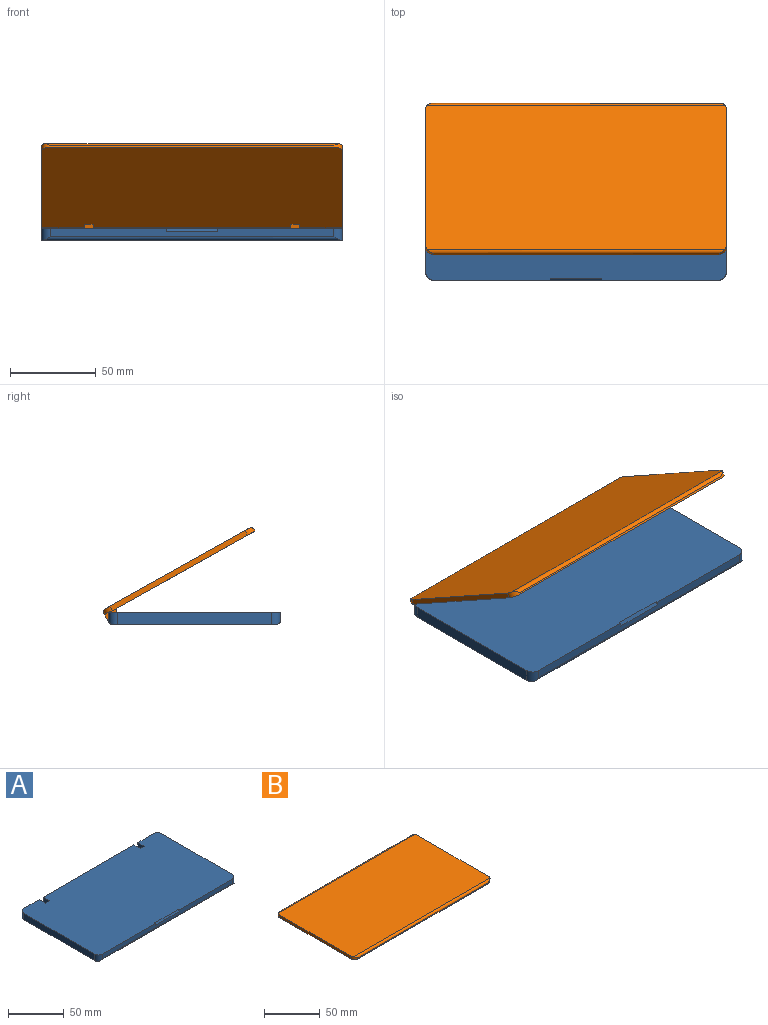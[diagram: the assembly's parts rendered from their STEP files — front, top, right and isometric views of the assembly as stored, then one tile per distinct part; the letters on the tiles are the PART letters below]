
ASSEMBLY  parts=2 mates=1
PART A: 52 faces, bbox 175x100x7 mm
  f0: plane 175x100mm, normal (0,0,1), area 17368.5mm2, adj f1,f2,f6,f7,f9,f11,f12,f13
  f1: plane 20x5mm, normal (0,1,0), area 100mm2, adj f0,f4,f12,f22
  f2: plane 115x5mm, normal (0,1,0), area 575mm2, adj f0,f3,f18,f23
  f3: cylinder r=2mm len=115mm, axis (-1,0,0), area 361.3mm2, adj f2,f10,f18,f23
  f4: cylinder r=2mm len=24mm, axis (-1,0,0), area 69.8mm2, adj f1,f10,f12,f22
  f5: cylinder r=2mm len=24mm, axis (-1,0,0), area 69.8mm2, adj f9,f10,f13,f19
  f6: plane 90x7mm, normal (1,0,0), area 630mm2, adj f0,f10,f13,f15
  f7: plane 165x5mm, normal (0,-1,0), area 765mm2, adj f0,f8,f14,f15,f24,f25,f26
  f8: cylinder r=2mm len=173mm, axis (-1,0,0), area 532.4mm2, adj f7,f10,f14,f15
  f9: plane 20x5mm, normal (0,1,0), area 100mm2, adj f0,f5,f13,f19
  f10: plane 175x96mm, normal (0,0,-1), area 16796.2mm2, adj f3,f4,f5,f6,f8,f11,f12,f13
  f11: plane 90x7mm, normal (-1,0,0), area 630mm2, adj f0,f10,f12,f14
  f12: cylinder r=5mm len=7mm, axis (0,0,1), area 51.4mm2, adj f0,f1,f4,f10,f11
  f13: cylinder r=5mm len=7mm, axis (0,0,1), area 51.4mm2, adj f0,f5,f6,f9,f10
  f14: cylinder r=5mm len=7mm, axis (0,0,1), area 51.4mm2, adj f0,f7,f8,f10,f11
  f15: cylinder r=5mm len=7mm, axis (0,0,1), area 51.4mm2, adj f0,f6,f7,f8,f10
  f16: cylinder r=2mm len=5mm, axis (-1,0,0), area 9.5mm2, adj f10,f17,f18,f19
  f17: plane 6.16x5mm, normal (0,0.82,0.58), area 37.7mm2, adj f0,f16,f18,f19
  f18: plane 8x7mm, normal (1,0,0), area 37.6mm2, adj f0,f2,f3,f16,f17
  f19: plane 8x7mm, normal (-1,0,0), area 37.6mm2, adj f0,f5,f9,f16,f17
  f20: cylinder r=2mm len=5mm, axis (-1,0,0), area 9.5mm2, adj f10,f21,f22,f23
  f21: plane 6.16x5mm, normal (0,0.82,0.58), area 37.7mm2, adj f0,f20,f22,f23
  f22: plane 8x7mm, normal (1,0,0), area 37.6mm2, adj f0,f1,f4,f20,f21
  f23: plane 8x7mm, normal (-1,0,0), area 37.6mm2, adj f0,f2,f3,f20,f21
  f24: plane 2x1mm, normal (-1,0,0), area 1mm2, adj f0,f7,f25
  f25: plane 30x2mm, normal (0,-0.89,0.45), area 67.1mm2, adj f0,f7,f24,f26
  f26: plane 2x1mm, normal (1,0,0), area 1mm2, adj f0,f7,f25
  f27: plane 173x96mm, normal (0,0,1), area 16561.4mm2, adj f31,f32,f33,f34,f36,f38,f39,f40
  f28: plane 173x98mm, normal (0,0,-1), area 16815.3mm2, adj f29,f30,f34,f35,f37,f38,f39,f40
  f29: plane 19x4mm, normal (0,-1,0), area 76mm2, adj f28,f32,f39,f47
  f30: plane 113x4mm, normal (0,-1,0), area 452mm2, adj f28,f31,f44,f48
  f31: cylinder r=1mm len=113mm, axis (-1,0,0), area 177.5mm2, adj f27,f30,f44,f48
  f32: cylinder r=1mm len=21.65mm, axis (-1,0,0), area 32.1mm2, adj f27,f29,f39,f47
  f33: cylinder r=1mm len=21.65mm, axis (-1,0,0), area 32.1mm2, adj f27,f37,f40,f45
  f34: plane 90x5mm, normal (-1,0,0), area 450mm2, adj f27,f28,f40,f42
  f35: plane 165x4mm, normal (0,1,0), area 620.4mm2, adj f28,f36,f41,f42,f49,f50,f51
  f36: cylinder r=1mm len=170.29mm, axis (-1,0,0), area 263.7mm2, adj f27,f35,f41,f42
  f37: plane 19x4mm, normal (0,-1,0), area 76mm2, adj f28,f33,f40,f45
  f38: plane 90x5mm, normal (1,0,0), area 450mm2, adj f27,f28,f39,f41
  f39: cylinder r=4mm len=5mm, axis (0,0,1), area 30.3mm2, adj f27,f28,f29,f32,f38
  f40: cylinder r=4mm len=5mm, axis (0,0,1), area 30.3mm2, adj f27,f28,f33,f34,f37
  f41: cylinder r=4mm len=5mm, axis (0,0,1), area 30.3mm2, adj f27,f28,f35,f36,f38
  f42: cylinder r=4mm len=5mm, axis (0,0,1), area 30.3mm2, adj f27,f28,f34,f35,f36
  f43: plane 7x5mm, normal (0,-0.82,-0.58), area 42.9mm2, adj f27,f28,f44,f45
  f44: plane 7.52x5mm, normal (-1,0,0), area 28.5mm2, adj f27,f28,f30,f31,f43
  f45: plane 7.52x5mm, normal (1,0,0), area 28.5mm2, adj f27,f28,f33,f37,f43
  f46: plane 7x5mm, normal (0,-0.82,-0.58), area 42.9mm2, adj f27,f28,f47,f48
  f47: plane 7.52x5mm, normal (-1,0,0), area 28.5mm2, adj f27,f28,f29,f32,f46
  f48: plane 7.52x5mm, normal (1,0,0), area 28.5mm2, adj f27,f28,f30,f31,f46
  f49: plane 1.24x0.62mm, normal (1,0,0), area 0.4mm2, adj f28,f35,f50
  f50: plane 32x1.24mm, normal (0,0.89,-0.45), area 44.2mm2, adj f28,f35,f49,f51
  f51: plane 1.24x0.62mm, normal (-1,0,0), area 0.4mm2, adj f28,f35,f50
PART B: 48 faces, bbox 175x100x10 mm
  f0: cylinder r=5.39mm len=24.9mm, axis (-1,0,0), area 97mm2, adj f3,f5,f14,f22
  f1: cylinder r=5.39mm len=115mm, axis (-1,0,0), area 471.3mm2, adj f3,f5,f17,f21
  f2: cylinder r=5.39mm len=24.9mm, axis (-1,0,0), area 97mm2, adj f3,f5,f13,f16
  f3: plane 175x96mm, normal (0,0,-1), area 16749.2mm2, adj f0,f1,f2,f4,f7,f8,f11,f12
  f4: plane 90x3mm, normal (1,0,0), area 270mm2, adj f3,f6,f12,f14
  f5: plane 165x6mm, normal (0,1,0), area 215mm2, adj f0,f1,f2,f9,f13,f14,f16,f17
  f6: plane 175x96mm, normal (0,0,1), area 16796.2mm2, adj f4,f8,f9,f10,f11,f12,f13,f14
  f7: plane 165x1mm, normal (0,-1,0), area 165mm2, adj f3,f10,f11,f12
  f8: plane 90x3mm, normal (-1,0,0), area 270mm2, adj f3,f6,f11,f13
  f9: cylinder r=2mm len=173mm, axis (-1,0,0), area 532.4mm2, adj f5,f6,f13,f14
  f10: cylinder r=2mm len=173mm, axis (-1,0,0), area 532.4mm2, adj f6,f7,f11,f12
  f11: cylinder r=5mm len=5mm, axis (0,0,-1), area 20mm2, adj f3,f6,f7,f8,f10
  f12: cylinder r=5mm len=5mm, axis (0,0,-1), area 20mm2, adj f3,f4,f6,f7,f10
  f13: cylinder r=5mm len=5mm, axis (0,0,-1), area 18.6mm2, adj f2,f3,f5,f6,f8,f9
  f14: cylinder r=5mm len=5mm, axis (0,0,-1), area 18.6mm2, adj f0,f3,f4,f5,f6,f9
  f15: cylinder r=1mm len=5mm, axis (-1,0,0), area 31.4mm2, adj f16,f17
  f16: plane 8x7.39mm, normal (-1,0,0), area 35.5mm2, adj f2,f3,f5,f15,f18,f19
  f17: plane 8x7.39mm, normal (1,0,0), area 35.5mm2, adj f1,f3,f5,f15,f18,f19
  f18: plane 6.16x5mm, normal (0,-0.82,-0.58), area 37.7mm2, adj f3,f16,f17,f19
  f19: cylinder r=2mm len=5mm, axis (-1,0,0), area 25.2mm2, adj f5,f16,f17,f18
  f20: cylinder r=1mm len=5mm, axis (-1,0,0), area 31.4mm2, adj f21,f22
  f21: plane 8x7.39mm, normal (-1,0,0), area 35.5mm2, adj f1,f3,f5,f20,f23,f24
  f22: plane 8x7.39mm, normal (1,0,0), area 35.5mm2, adj f0,f3,f5,f20,f23,f24
  f23: cylinder r=2mm len=5mm, axis (-1,0,0), area 25.2mm2, adj f5,f21,f22,f24
  f24: plane 6.16x5mm, normal (0,-0.82,-0.58), area 37.7mm2, adj f3,f21,f22,f23
  f25: cylinder r=1mm len=170.29mm, axis (-1,0,0), area 212.5mm2, adj f26,f28,f29,f30,f31,f34,f39,f40
  f26: plane 4.27x3mm, normal (0,-1,0), area 12.8mm2, adj f25,f27,f41,f42
  f27: cylinder r=2mm len=3mm, axis (-1,0,0), area 10mm2, adj f26,f41,f42,f43
  f28: plane 4.27x3mm, normal (0,-1,0), area 12.8mm2, adj f25,f44,f45,f46
  f29: cylinder r=6.39mm len=24.92mm, axis (-1,0,0), area 76.3mm2, adj f25,f32,f40,f46
  f30: cylinder r=6.39mm len=117mm, axis (-1,0,0), area 372.3mm2, adj f25,f32,f42,f45
  f31: cylinder r=6.39mm len=24.92mm, axis (-1,0,0), area 76.3mm2, adj f25,f32,f39,f41
  f32: plane 173x94.82mm, normal (0,0,1), area 16376.4mm2, adj f29,f30,f31,f33,f35,f36,f37,f38
  f33: plane 90x1mm, normal (-1,0,0), area 90mm2, adj f32,f34,f38,f40
  f34: plane 173x96mm, normal (0,0,-1), area 16603mm2, adj f25,f33,f35,f36,f37,f38,f39,f40
  f35: plane 90x1mm, normal (1,0,0), area 90mm2, adj f32,f34,f37,f39
  f36: cylinder r=1mm len=170.29mm, axis (-1,0,0), area 263.7mm2, adj f32,f34,f37,f38
  f37: cylinder r=4mm len=4mm, axis (0,0,-1), area 5.2mm2, adj f32,f34,f35,f36
  f38: cylinder r=4mm len=4mm, axis (0,0,-1), area 5.2mm2, adj f32,f33,f34,f36
  f39: cylinder r=4mm len=3.95mm, axis (0,0,-1), area 3.6mm2, adj f25,f31,f32,f34,f35
  f40: cylinder r=4mm len=3.95mm, axis (0,0,-1), area 3.6mm2, adj f25,f29,f32,f33,f34
  f41: plane 6.48x5.55mm, normal (1,0,0), area 22.3mm2, adj f25,f26,f27,f31,f32,f43
  f42: plane 6.48x5.55mm, normal (-1,0,0), area 22.3mm2, adj f25,f26,f27,f30,f32,f43
  f43: plane 5.17x3.67mm, normal (0,0.82,0.58), area 19mm2, adj f27,f32,f41,f42
  f44: cylinder r=2mm len=3mm, axis (-1,0,0), area 10mm2, adj f28,f45,f46,f47
  f45: plane 6.48x5.55mm, normal (1,0,0), area 22.3mm2, adj f25,f28,f30,f32,f44,f47
  f46: plane 6.48x5.55mm, normal (-1,0,0), area 22.3mm2, adj f25,f28,f29,f32,f44,f47
  f47: plane 5.17x3.67mm, normal (0,0.82,0.58), area 19mm2, adj f32,f44,f45,f46
PLACE A at identity fixed
PLACE B rot(axis=(-1,0,0),29.2deg) t=(0,8.54,22.78)mm
MATE revolute B.f0 <-> A.f3  axis (-1,0,0) through (62.5,48,-5)mm
